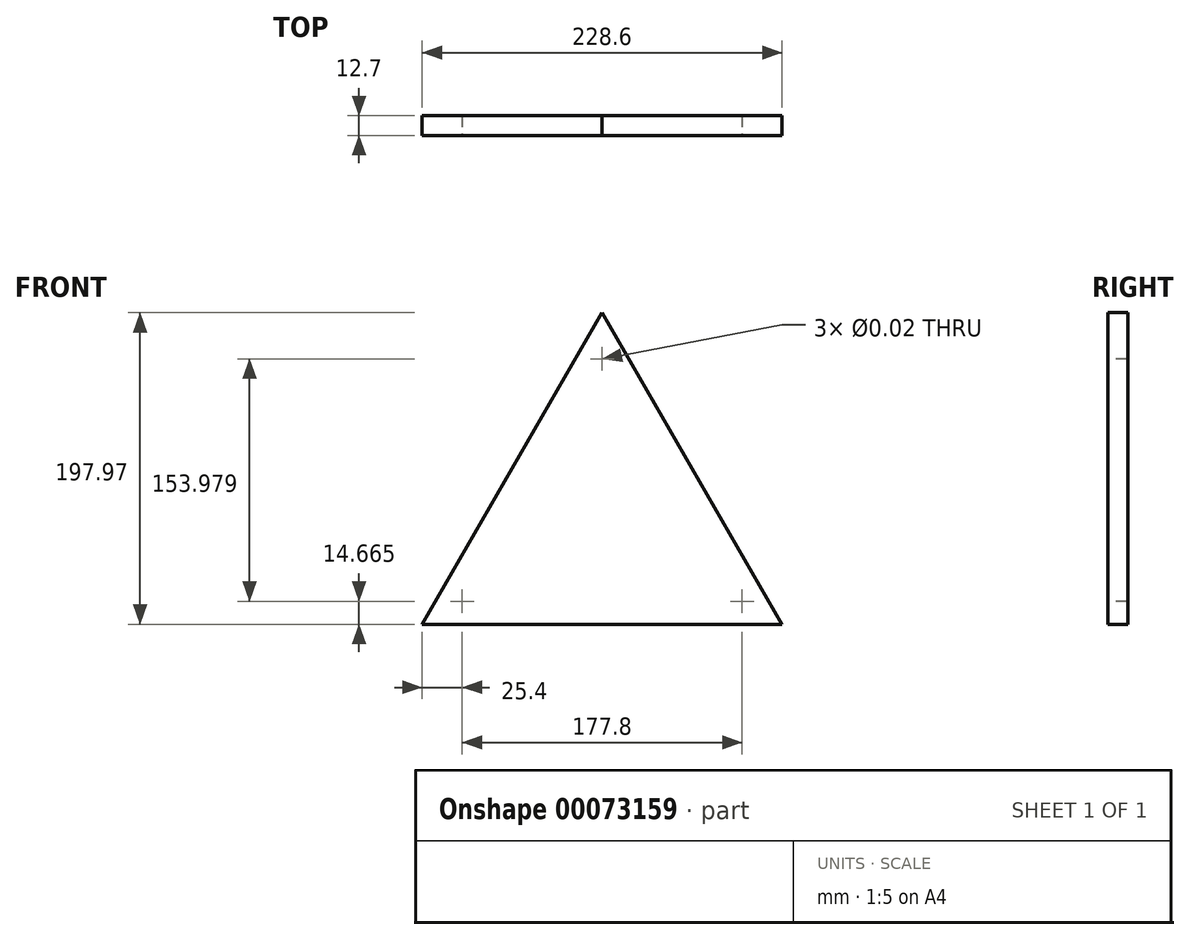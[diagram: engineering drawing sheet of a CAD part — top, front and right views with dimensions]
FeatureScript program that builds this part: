
annotation { "Feature Type Name" : "Feature", "Feature Type Description" : "" }
export const myFeature = defineFeature(function(context is Context, id is Id, definition is map)
    precondition{}
    {
        {
            var Q0;
            Q0=qCreatedBy(makeId("Front.planeOp"),FACE);
            var sketch = newSketch(context, id + "F0", { "sketchPlane" : qUnion([Q0])});
            skLineSegment(sketch, "E0", {"start": v(0, 197.97) * mm, "end": v(-114.3, 0) * mm});
            skLineSegment(sketch, "E1", {"start": v(-114.3, 0) * mm, "end": v(114.3, 0) * mm});
            skLineSegment(sketch, "E2", {"start": v(114.3, 0) * mm, "end": v(0, 197.97) * mm});
            skSolve(sketch);
        }
        {
            var Q0;
            Q0=makeQuery(id+"F0.imprint","IMPRINT",FACE,{"disambiguationData":[TD([[makeQuery(id+"F0.imprint","IMPRINT",EDGE,{"derivedFrom":sQuery(id+"F0.wireOp",EDGE,"E0")}),1.0]])]});
            extrude(context, id + "F1", {"entities" : qUnion([Q0]), "depth" : 12.7 * mm});
        }
        {
            var Q0;
            Q0=makeQuery(id+"F1.opExtrude","CAP_FACE",FACE,{"disambiguationData":[OSD([sQuery(id+"F0.wireOp",EDGE,"E0"),sQuery(id+"F0.wireOp",EDGE,"E1"),sQuery(id+"F0.wireOp",EDGE,"E2")])],"isStart":false});
            var sketch = newSketch(context, id + "F2", { "sketchPlane" : qUnion([Q0])});
            skCircle(sketch, "E3", {"center": v(0, 168.64) * mm, "radius": 7.94 * mm});
            skCircle(sketch, "E4", {"center": v(-88.9, 14.66) * mm, "radius": 7.94 * mm});
            skCircle(sketch, "E5", {"center": v(88.9, 14.66) * mm, "radius": 7.94 * mm});
            skLineSegment(sketch, "E6", {"start": v(88.9, 14.66) * mm, "end": v(114.3, 0) * mm, "construction": true});
            skLineSegment(sketch, "E7", {"start": v(-88.9, 14.66) * mm, "end": v(-114.3, 0) * mm, "construction": true});
            skLineSegment(sketch, "E8", {"start": v(0, 168.64) * mm, "end": v(0, 197.97) * mm, "construction": true});
            skSolve(sketch);
        }
        {
            var Q0;
            Q0=sQuery(id+"F2.wireOp",VERTEX,"E3.center");
            var Q1;
            Q1=sQuery(id+"F2.wireOp",VERTEX,"E7.start");
            var Q2;
            Q2=sQuery(id+"F2.wireOp",VERTEX,"E5.center");
            var Q3;
            Q3=makeQuery(id+"F1.opExtrude","SWEPT_BODY",BODY,{"disambiguationData":[OSD([sQuery(id+"F0.wireOp",EDGE,"E0"),sQuery(id+"F0.wireOp",EDGE,"E1"),sQuery(id+"F0.wireOp",EDGE,"E2")])]});
            hole(context, id + "F3", {"style" : HoleStyle.SIMPLE, "holeDiameter" : 5 / 203.2 * mm, "endStyle" : HoleEndStyle.THROUGH, "locations" : qUnion([Q0, Q1, Q2]), "scope" : qUnion([Q3])});
        }
    });
